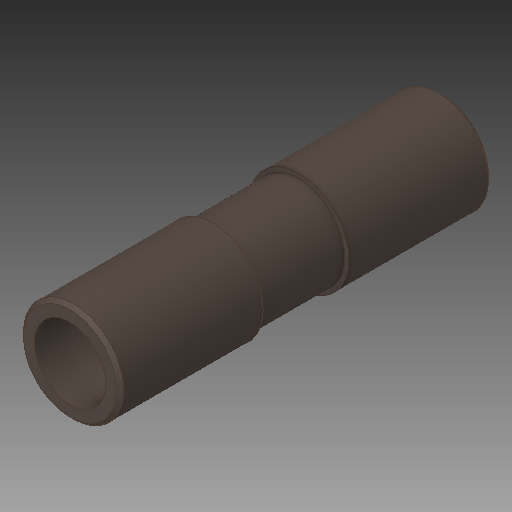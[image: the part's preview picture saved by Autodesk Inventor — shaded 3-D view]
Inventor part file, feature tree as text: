
AUTODESK INVENTOR PART (.ipt)
format: ipt  version: 2018 (Build 220112000, 112)  size: 111,616 bytes
history: native  units: in
note: dims shown in document units (in); Inventor stores cm internally (conversion verified against a paired STEP export)
features: chamfer x1
ambient origin geometry x8: Origin, YZ Plane, XZ Plane, XY Plane, X Axis, Y Axis, Z Axis, Center Point
bodies: Solid1 (feature_tree)
feature tree (1):
  chamfer  "Chamfer1"  [1 undecoded]
note: 1 required parameter value undecoded (feature->parameter linkage not recoverable at this tier; creation-order binding heuristic only, values carry confidence <= 0.55)
